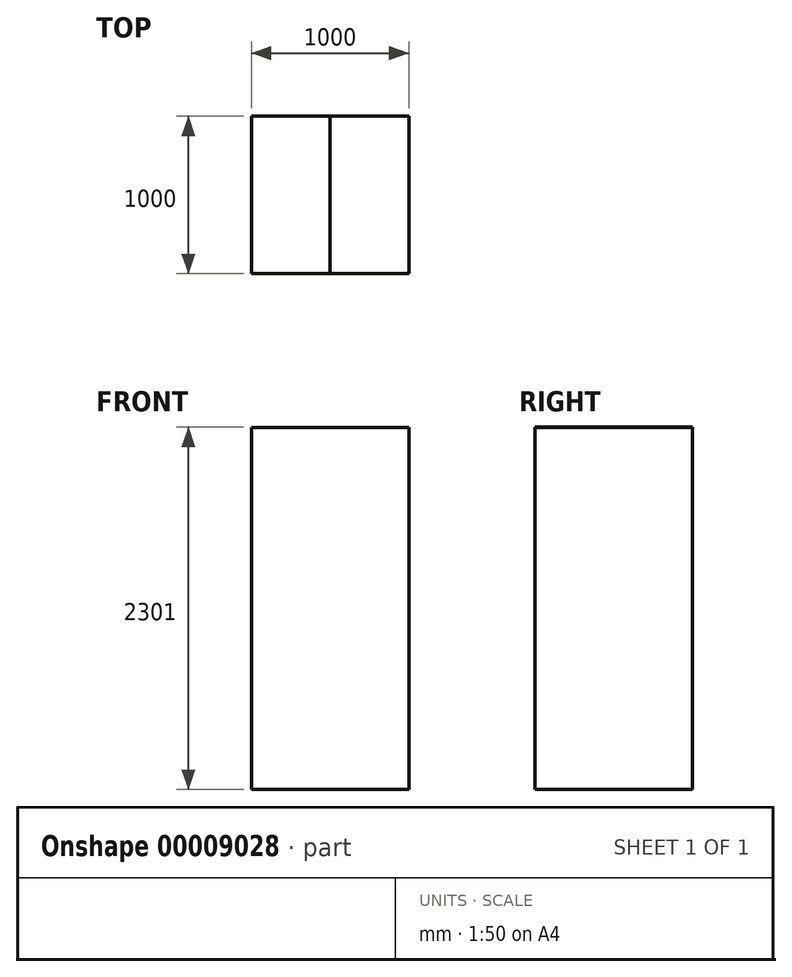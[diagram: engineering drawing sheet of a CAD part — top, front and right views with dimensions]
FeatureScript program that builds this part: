
annotation { "Feature Type Name" : "Feature", "Feature Type Description" : "" }
export const myFeature = defineFeature(function(context is Context, id is Id, definition is map)
    precondition{}
    {
        {
            var Q0;
            Q0=qCreatedBy(makeId("Top.planeOp"),FACE);
            var sketch = newSketch(context, id + "F0", { "sketchPlane" : qUnion([Q0])});
            skLineSegment(sketch, "E0.bottom", {"start": v(0, 0) * mm, "end": v(-1000, 0) * mm});
            skLineSegment(sketch, "E0.top", {"start": v(0, 1000) * mm, "end": v(-1000, 1000) * mm});
            skLineSegment(sketch, "E0.left", {"start": v(0, 0) * mm, "end": v(0, 1000) * mm});
            skLineSegment(sketch, "E0.right", {"start": v(-1000, 0) * mm, "end": v(-1000, 1000) * mm});
            skSolve(sketch);
        }
        {
            var Q0;
            Q0=makeQuery(id+"F0.imprint","IMPRINT",FACE,{"disambiguationData":[TD([[makeQuery(id+"F0.imprint","IMPRINT",EDGE,{"derivedFrom":sQuery(id+"F0.wireOp",EDGE,"E0.bottom")}),-1.0]])]});
            extrude(context, id + "F1", {"entities" : qUnion([Q0]), "depth" : 2300 * mm});
        }
        {
            var Q0;
            Q0=makeQuery(id+"F1.opExtrude","CAP_FACE",FACE,{"disambiguationData":[OSD([sQuery(id+"F0.wireOp",EDGE,"E0.bottom"),sQuery(id+"F0.wireOp",EDGE,"E0.top"),sQuery(id+"F0.wireOp",EDGE,"E0.left"),sQuery(id+"F0.wireOp",EDGE,"E0.right")])],"isStart":false});
            var sketch = newSketch(context, id + "F2", { "sketchPlane" : qUnion([Q0])});
            skLineSegment(sketch, "E1.bottom", {"start": v(-500, 0) * mm, "end": v(-499, 0) * mm});
            skLineSegment(sketch, "E1.top", {"start": v(-500, 1000) * mm, "end": v(-499, 1000) * mm});
            skLineSegment(sketch, "E1.left", {"start": v(-500, 0) * mm, "end": v(-500, 1000) * mm});
            skLineSegment(sketch, "E1.right", {"start": v(-499, 0) * mm, "end": v(-499, 1000) * mm});
            skSolve(sketch);
        }
        {
            var Q0;
            Q0 = qSketchRegion(id + "F2", true);
            extrude(context, id + "F3", {"entities" : qUnion([Q0]), "operationType" : NewBodyOperationType.ADD, "depth" : 1 * mm});
        }
    });
